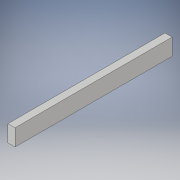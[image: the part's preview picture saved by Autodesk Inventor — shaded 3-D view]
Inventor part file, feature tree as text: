
AUTODESK INVENTOR PART (.ipt)
format: ipt  version: 2017 (Build 210142000, 142)  size: 90,112 bytes
history: native  units: in
note: dims shown in document units (in); Inventor stores cm internally (conversion verified against a paired STEP export)
features: extrude x1, sketch x1
ambient origin geometry x8: Origin, YZ Plane, XZ Plane, XY Plane, X Axis, Y Axis, Z Axis, Center Point
bodies: Solid1 (feature_tree)
feature tree (2):
  extrude  "Extrusion1"  Depth=33.0in
  sketch  "Sketch1"  dims[d0=1.5in d1=33.0in d2=3.5in d3=0.0in]
